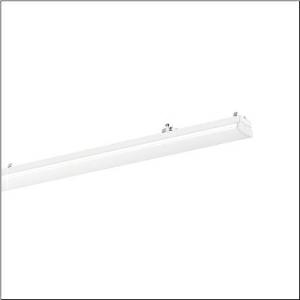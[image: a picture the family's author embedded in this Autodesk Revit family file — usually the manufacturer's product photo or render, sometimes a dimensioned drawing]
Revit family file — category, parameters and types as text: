
# Revit family: licross_r__21_recessed_opal_mo_52te1d7n46xg_cd2b
name_source: partatom
category: Lighting Fixtures
units: mm (PartAtom-declared; Revit-internal decimal feet)

## family parameters
Cut with Voids When Loaded = No
Host = Face
Light Source = No
Part Type = Normal
Room Calculation Point = No
Round Connector Dimension = Use Diameter
Shared = No

## types (1)
- Licross® 21 recessed opal MO (1 x LED, 6200 lm, 34.9 W, 4000K)
    Apparent Load = 35 VA
    CIE Flux Codes = 44 73 91 87 100
    Color Rendering = 80
    Color Temperature = 4000K
    Default Elevation = 1800 mm
    Description = Licross® 21 recessed opal MO, luminaire insert, of sheet steel, galvanised, coil coated, white, length: 1.500mm, width: 66mm, height: 67mm, LED rated luminous flux: 6.200lm, light colour: 840, control gear: ON/OFF, with plug, 3-pole, with phase selection, mains connection: 220..240V, AC, 50/60Hz, rated input power: 35W, internal wiring halogen-free, primary optical cover: cover, of PMMA, light emission: direct with ceiling illumination distribution, primary light characteristic: symmetric, protection rating (complete): IP54, insulation class (complete): insulation class I (protective earthing), certification: CE, ENEC, VDE, UKCA, protection symbol: D if used in an environment with non-conductive dust loads with corresponding accessories, impact resistance: IK06, permissible ambient temperature for indoor applications: -35..+50°C, corresponds to IFS (International Featured Standards) requirements for safety and quality in the food industry, reducing of maximum allowable ambient temperature of 5°C with ceiling mounting, LABS conformity tested according to VDMA 24364:2018-05, packaging unit: 1 piece
    Height = 83 mm
    Lamp = 1 x LED
    Lamp Light Flux = 6200 lm
    Lamp Power = 34.9 W
    Lamp count = 1
    Length = 1500 mm
    Luminous efficacy = 178 lm/W
    Manufacturer = Siteco
    ModVariant = No
    Model = 52TE1D7N46XG
    Mounting Place = Ceiling
    Mounting Type = Pendant
    Number of Poles = 1
    OnlyDefault = Yes
    Power Factor = 1
    Product Name = Licross® 21 recessed opal MO
    Product group = luminaire insert | ceiling pendant
    ProductGroupID = 902
    Protection Class = Protection class I
    Protection Degree = IP 54
    RLX_Detail_Level = 1
    RLX_Emergency_Light_Flux = 0 lm
    RLX_Emergency_Type = 0
    RLX_Emergency_Type_DB = No
    RlxData = <blob elided: 23129 chars, md5=b0307a3b>
    Socket = socket
    Standby Power = 0 W
    System Light Flux = 6200 lm
    System Power = 35 W
    Type Comments = Product without accessories
    Type Image = l_1313666.jpg
    URL = http://relux.com
    VarID = ---
    Voltage = 0 V
    Weight = 0.00 kg
    Width = 76 mm

## geometry (parser evidence)
native form markers: Blend x4, Sweep x11
no freeform markers — native parametric forms only
